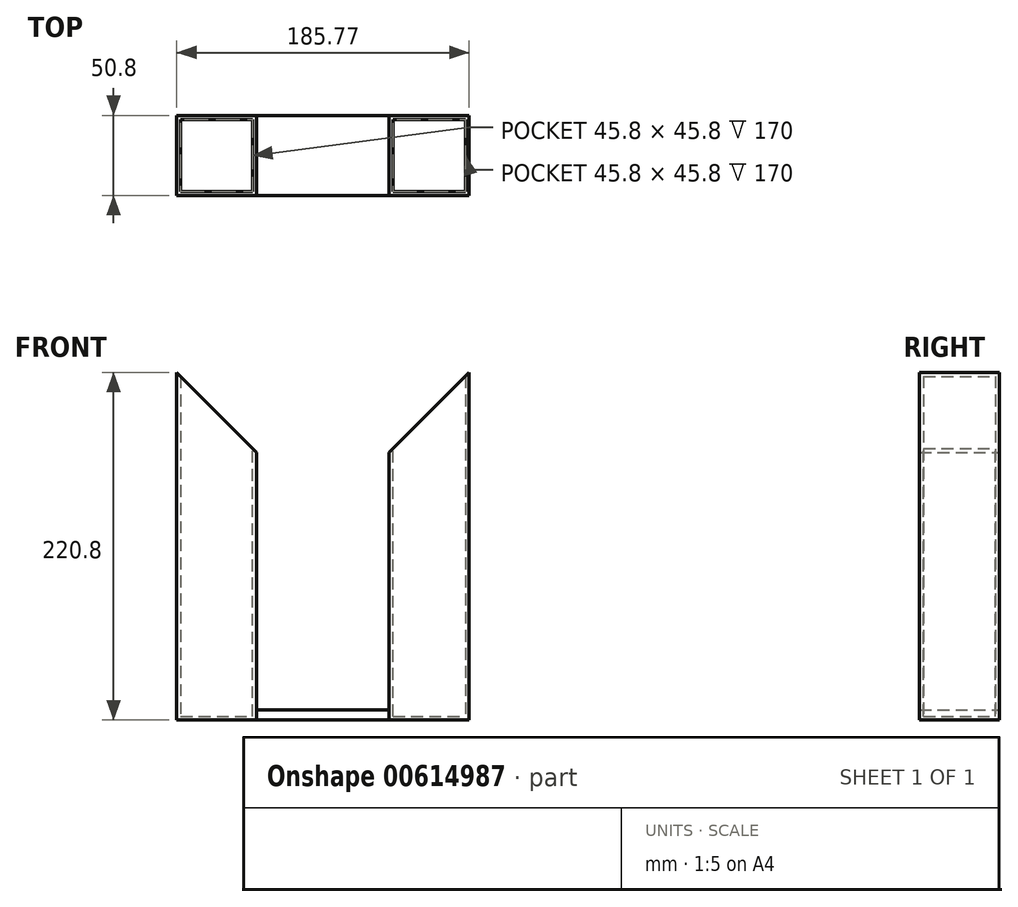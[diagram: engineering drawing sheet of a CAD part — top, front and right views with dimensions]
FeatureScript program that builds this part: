
annotation { "Feature Type Name" : "Feature", "Feature Type Description" : "" }
export const myFeature = defineFeature(function(context is Context, id is Id, definition is map)
    precondition{}
    {
        {
            var Q0;
            Q0=qCreatedBy(makeId("Front.planeOp"),FACE);
            var sketch = newSketch(context, id + "F0", { "sketchPlane" : qUnion([Q0])});
            skLineSegment(sketch, "E0.bottom", {"start": v(-71.78, 0) * mm, "end": v(131.42, 0) * mm});
            skLineSegment(sketch, "E0.top", {"start": v(-71.78, 170) * mm, "end": v(131.42, 170) * mm});
            skLineSegment(sketch, "E0.left", {"start": v(-71.78, 0) * mm, "end": v(-71.78, 170) * mm});
            skLineSegment(sketch, "E0.right", {"start": v(131.42, 0) * mm, "end": v(131.42, 170) * mm});
            skLineSegment(sketch, "E1", {"start": v(-71.78, 170) * mm, "end": v(-71.78, 400.24) * mm, "construction": true});
            skLineSegment(sketch, "E2", {"start": v(131.42, 170) * mm, "end": v(131.42, 404.73) * mm, "construction": true});
            skLineSegment(sketch, "E3", {"start": v(29.82, 170) * mm, "end": v(29.82, 271.6) * mm, "construction": true});
            skCircle(sketch, "E4", {"center": v(29.82, 271.6) * mm, "radius": 101.6 * mm});
            skLineSegment(sketch, "E5", {"start": v(-71.78, 271.6) * mm, "end": v(131.42, 271.6) * mm, "construction": true});
            skLineSegment(sketch, "E6", {"start": v(-71.78, 271.6) * mm, "end": v(29.82, 170) * mm, "construction": true});
            skLineSegment(sketch, "E7", {"start": v(29.82, 170) * mm, "end": v(131.42, 271.6) * mm, "construction": true});
            skLineSegment(sketch, "E8", {"start": v(-63.06, 220.8) * mm, "end": v(-12.26, 170) * mm});
            skLineSegment(sketch, "E9", {"start": v(71.9, 170) * mm, "end": v(122.7, 220.8) * mm});
            skPoint(sketch, "E10.orphan", {"position": v(29.82, 373.2) * mm});
            skLineSegment(sketch, "E11", {"start": v(224.64, 220.8) * mm, "end": v(-141.53, 220.8) * mm, "construction": true});
            skPoint(sketch, "E11.endSnap0", {"position": v(29.82, 220.8) * mm});
            skLineSegment(sketch, "E12", {"start": v(-63.06, 220.8) * mm, "end": v(-63.06, 0) * mm});
            skLineSegment(sketch, "E13", {"start": v(122.7, 220.8) * mm, "end": v(122.7, 0) * mm});
            skLineSegment(sketch, "E14", {"start": v(-63.06, 0) * mm, "end": v(-12.26, 0) * mm});
            skLineSegment(sketch, "E15", {"start": v(-12.26, 0) * mm, "end": v(-12.26, 170) * mm});
            skLineSegment(sketch, "E16.MirrorCS", {"start": v(71.9, 0) * mm, "end": v(71.9, 170) * mm});
            skLineSegment(sketch, "E17.MirrorCS", {"start": v(122.7, 0) * mm, "end": v(71.9, 0) * mm});
            skPoint(sketch, "E18.orphan", {"position": v(0, 157.74) * mm});
            skLineSegment(sketch, "E19.trimOffspring", {"start": v(71.9, 179.13) * mm, "end": v(71.9, 271.6) * mm});
            skLineSegment(sketch, "E20.trimOffspring", {"start": v(-12.26, 179.13) * mm, "end": v(-12.26, 271.6) * mm});
            skLineSegment(sketch, "E21.bottom", {"start": v(-63.06, 0) * mm, "end": v(122.7, 0) * mm});
            skLineSegment(sketch, "E22.top", {"start": v(-63.06, 6.35) * mm, "end": v(122.7, 6.35) * mm});
            skLineSegment(sketch, "E22.left", {"start": v(-63.06, 0) * mm, "end": v(-63.06, 6.35) * mm});
            skLineSegment(sketch, "E22.right", {"start": v(122.7, 0) * mm, "end": v(122.7, 6.35) * mm});
            skSolve(sketch);
        }
        {
            var Q0;
            {var subQ0=sQuery(id+"F0.wireOp",EDGE,"E8");var subQ3=sQuery(id+"F0.wireOp",EDGE,"E12");var subQ5=makeQuery(id+"F0.imprint","INTERSECT",VERTEX,{"derivedFrom":[subQ0,subQ3]});Q0=makeQuery(id+"F0.imprint","IMPRINT",FACE,{"disambiguationData":[TD([[makeQuery(id+"F0.imprint","IMPRINT",EDGE,{"disambiguationData":[TD([[subQ5,-1.0]])],"derivedFrom":subQ0}),-1.0]])]});}
            var Q1;
            {var subQ0=sQuery(id+"F0.wireOp",EDGE,"E9");var subQ3=sQuery(id+"F0.wireOp",EDGE,"E13");var subQ6=makeQuery(id+"F0.imprint","INTERSECT",VERTEX,{"derivedFrom":[subQ0,subQ3]});Q1=makeQuery(id+"F0.imprint","IMPRINT",FACE,{"disambiguationData":[TD([[makeQuery(id+"F0.imprint","IMPRINT",EDGE,{"disambiguationData":[TD([[subQ6,1.0]])],"derivedFrom":subQ0}),-1.0]])]});}
            var Q2;
            {var subQ0=sQuery(id+"F0.wireOp",EDGE,"E16.MirrorCS");Q2=makeQuery(id+"F0.imprint","IMPRINT",FACE,{"disambiguationData":[TD([[makeQuery(id+"F0.imprint","IMPRINT",EDGE,{"derivedFrom":subQ0}),-1.0]])]});}
            var Q3;
            {var subQ0=sQuery(id+"F0.wireOp",EDGE,"E15");Q3=makeQuery(id+"F0.imprint","IMPRINT",FACE,{"disambiguationData":[TD([[makeQuery(id+"F0.imprint","IMPRINT",EDGE,{"derivedFrom":subQ0}),1.0]])]});}
            extrude(context, id + "F1", {"entities" : qUnion([Q0, Q1, Q2, Q3]), "depth" : 50.8 * mm, "offsetDistance" : 25 * mm});
        }
        {
            var Q0;
            Q0=makeQuery(id+"F1.opExtrude","SWEPT_FACE",FACE,{"disambiguationData":[OSD([sQuery(id+"F0.wireOp",EDGE,"E8")])]});
            var Q1;
            Q1=makeQuery(id+"F1.opExtrude","SWEPT_FACE",FACE,{"disambiguationData":[OSD([sQuery(id+"F0.wireOp",EDGE,"E9")])]});
            shell(context, id + "F2", {"entities" : qUnion([Q0, Q1]), "thickness" : 2.5 * mm});
        }
        {
            var Q0;
            {var subQ0=sQuery(id+"F0.wireOp",EDGE,"E21.bottom");var subQ1=sQuery(id+"F0.wireOp",EDGE,"E15");var subQ2=makeQuery(id+"F0.imprint","INTERSECT",VERTEX,{"derivedFrom":[subQ1,subQ0]});Q0=makeQuery(id+"F0.imprint","IMPRINT",FACE,{"disambiguationData":[TD([[makeQuery(id+"F0.imprint","IMPRINT",EDGE,{"disambiguationData":[TD([[subQ2,-1.0]])],"derivedFrom":subQ1}),-1.0]])]});}
            var Q1;
            {var subQ5=sQuery(id+"F0.wireOp",EDGE,"E22.left");Q1=makeQuery(id+"F0.imprint","IMPRINT",FACE,{"disambiguationData":[TD([[makeQuery(id+"F0.imprint","IMPRINT",EDGE,{"derivedFrom":subQ5}),-1.0]])]});}
            var Q2;
            {var subQ5=sQuery(id+"F0.wireOp",EDGE,"E22.right");Q2=makeQuery(id+"F0.imprint","IMPRINT",FACE,{"disambiguationData":[TD([[makeQuery(id+"F0.imprint","IMPRINT",EDGE,{"derivedFrom":subQ5}),1.0]])]});}
            extrude(context, id + "F3", {"entities" : qUnion([Q0, Q1, Q2]), "depth" : 50.8 * mm, "offsetDistance" : 25 * mm});
        }
    });
